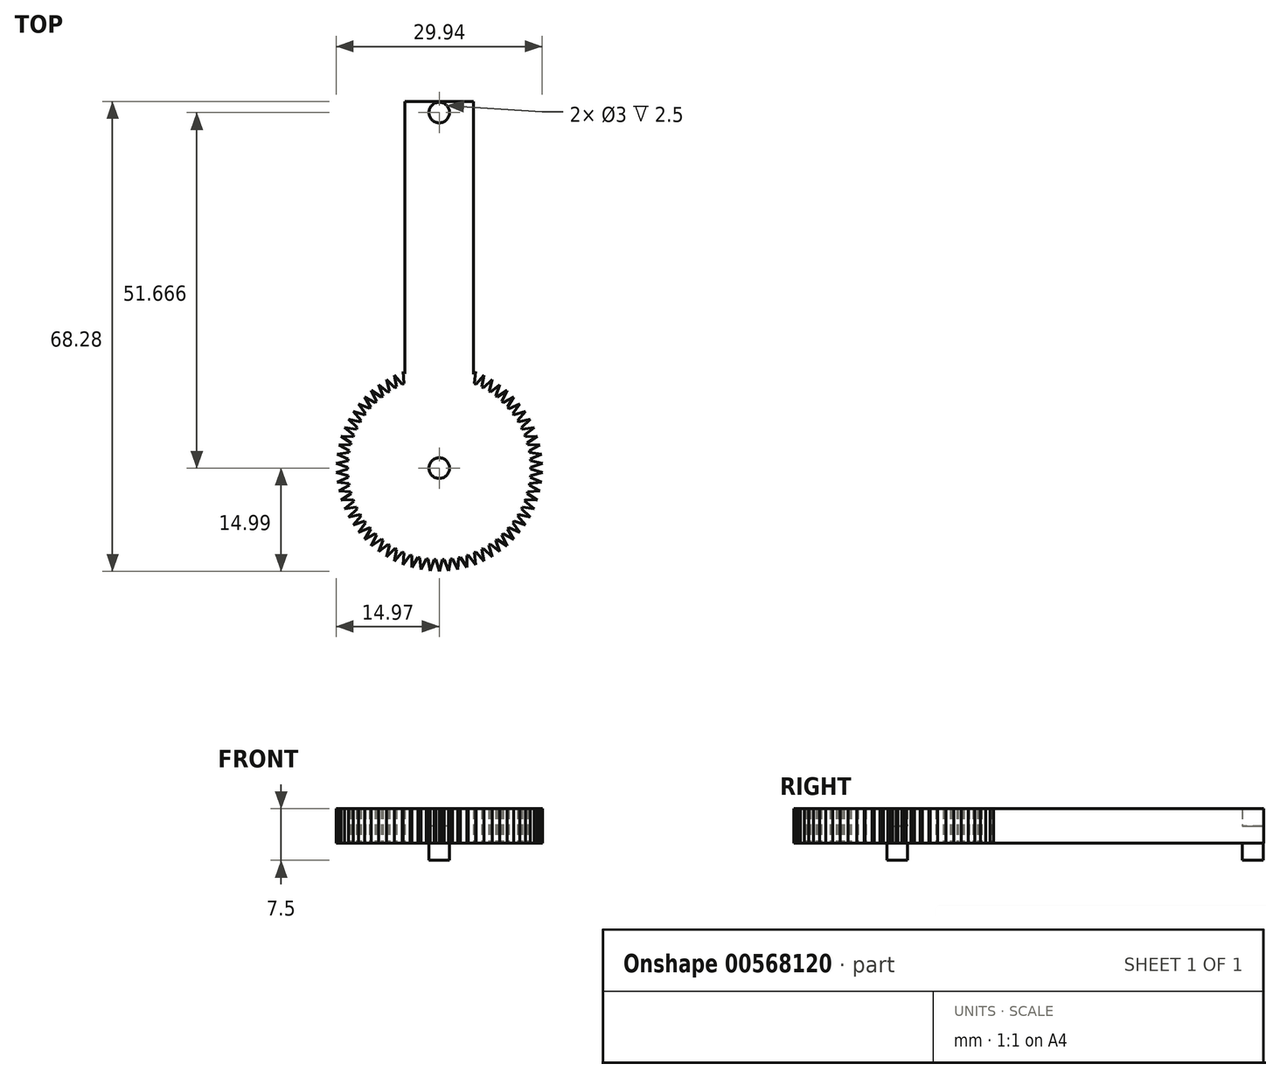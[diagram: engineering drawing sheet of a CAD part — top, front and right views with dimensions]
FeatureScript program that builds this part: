
annotation { "Feature Type Name" : "Feature", "Feature Type Description" : "" }
export const myFeature = defineFeature(function(context is Context, id is Id, definition is map)
    precondition{}
    {
        {
            var Q0;
            Q0=qCreatedBy(makeId("Top.planeOp"),FACE);
            var sketch = newSketch(context, id + "F0", { "sketchPlane" : qUnion([Q0])});
            skLineSegment(sketch, "E0.bottom", {"start": v(-5.03, 53.29) * mm, "end": v(4.97, 53.29) * mm});
            skLineSegment(sketch, "E0.left", {"start": v(-5.03, 53.29) * mm, "end": v(-5.03, 13.29) * mm});
            skLineSegment(sketch, "E0.right", {"start": v(4.97, 53.29) * mm, "end": v(4.97, 13.29) * mm});
            skCircle(sketch, "E1", {"center": v(0, -0.01) * mm, "radius": 15 * mm});
            skLineSegment(sketch, "E2.2.2", {"start": v(-2.84, 13) * mm, "end": v(-3.29, 12.92) * mm});
            skLineSegment(sketch, "E2.3.2", {"start": v(-3.99, 12.7) * mm, "end": v(-4.43, 12.57) * mm});
            skLineSegment(sketch, "E2.4.0", {"start": v(-5.27, 14.03) * mm, "end": v(-4.23, 12.61) * mm});
            skLineSegment(sketch, "E2.4.1", {"start": v(-5.27, 14.03) * mm, "end": v(-5.11, 12.28) * mm});
            skLineSegment(sketch, "E2.4.2", {"start": v(-5.11, 12.28) * mm, "end": v(-5.54, 12.12) * mm});
            skLineSegment(sketch, "E2.5.0", {"start": v(-6.5, 13.5) * mm, "end": v(-5.35, 12.18) * mm});
            skLineSegment(sketch, "E2.5.1", {"start": v(-6.5, 13.5) * mm, "end": v(-6.2, 11.78) * mm});
            skLineSegment(sketch, "E2.5.2", {"start": v(-6.2, 11.78) * mm, "end": v(-6.6, 11.58) * mm});
            skLineSegment(sketch, "E2.6.0", {"start": v(-7.69, 12.87) * mm, "end": v(-6.42, 11.66) * mm});
            skLineSegment(sketch, "E2.6.1", {"start": v(-7.69, 12.87) * mm, "end": v(-7.22, 11.17) * mm});
            skLineSegment(sketch, "E2.6.2", {"start": v(-7.22, 11.17) * mm, "end": v(-7.62, 10.94) * mm});
            skLineSegment(sketch, "E2.7.0", {"start": v(-8.8, 12.13) * mm, "end": v(-7.44, 11.03) * mm});
            skLineSegment(sketch, "E2.7.1", {"start": v(-8.8, 12.13) * mm, "end": v(-8.2, 10.48) * mm});
            skLineSegment(sketch, "E2.7.2", {"start": v(-8.2, 10.48) * mm, "end": v(-8.57, 10.21) * mm});
            skLineSegment(sketch, "E2.8.0", {"start": v(-9.86, 11.29) * mm, "end": v(-8.4, 10.32) * mm});
            skLineSegment(sketch, "E2.8.1", {"start": v(-9.86, 11.29) * mm, "end": v(-9.1, 9.7) * mm});
            skLineSegment(sketch, "E2.8.2", {"start": v(-9.1, 9.7) * mm, "end": v(-9.45, 9.4) * mm});
            skLineSegment(sketch, "E2.9.0", {"start": v(-10.83, 10.36) * mm, "end": v(-9.29, 9.53) * mm});
            skLineSegment(sketch, "E2.9.1", {"start": v(-10.83, 10.36) * mm, "end": v(-9.94, 8.85) * mm});
            skLineSegment(sketch, "E2.9.2", {"start": v(-9.94, 8.85) * mm, "end": v(-10.25, 8.52) * mm});
            skLineSegment(sketch, "E2.10.0", {"start": v(-11.72, 9.34) * mm, "end": v(-10.1, 8.66) * mm});
            skLineSegment(sketch, "E2.10.1", {"start": v(-11.72, 9.34) * mm, "end": v(-10.69, 7.92) * mm});
            skLineSegment(sketch, "E2.10.2", {"start": v(-10.69, 7.92) * mm, "end": v(-10.97, 7.57) * mm});
            skLineSegment(sketch, "E2.11.0", {"start": v(-12.5, 8.26) * mm, "end": v(-10.84, 7.72) * mm});
            skLineSegment(sketch, "E2.11.1", {"start": v(-12.5, 8.26) * mm, "end": v(-11.36, 6.93) * mm});
            skLineSegment(sketch, "E2.11.2", {"start": v(-11.36, 6.93) * mm, "end": v(-11.6, 6.55) * mm});
            skLineSegment(sketch, "E2.12.0", {"start": v(-13.2, 7.1) * mm, "end": v(-11.49, 6.71) * mm});
            skLineSegment(sketch, "E2.12.1", {"start": v(-13.2, 7.1) * mm, "end": v(-11.93, 5.89) * mm});
            skLineSegment(sketch, "E2.12.2", {"start": v(-11.93, 5.89) * mm, "end": v(-12.15, 5.49) * mm});
            skLineSegment(sketch, "E2.13.0", {"start": v(-13.78, 5.9) * mm, "end": v(-12.04, 5.66) * mm});
            skLineSegment(sketch, "E2.13.1", {"start": v(-13.78, 5.9) * mm, "end": v(-12.41, 4.8) * mm});
            skLineSegment(sketch, "E2.13.2", {"start": v(-12.41, 4.8) * mm, "end": v(-12.6, 4.37) * mm});
            skLineSegment(sketch, "E2.14.0", {"start": v(-14.25, 4.63) * mm, "end": v(-12.5, 4.56) * mm});
            skLineSegment(sketch, "E2.14.1", {"start": v(-14.25, 4.63) * mm, "end": v(-12.8, 3.66) * mm});
            skLineSegment(sketch, "E2.14.2", {"start": v(-12.8, 3.66) * mm, "end": v(-12.93, 3.23) * mm});
            skLineSegment(sketch, "E2.15.0", {"start": v(-14.61, 3.34) * mm, "end": v(-12.86, 3.42) * mm});
            skLineSegment(sketch, "E2.15.1", {"start": v(-14.61, 3.34) * mm, "end": v(-13.07, 2.5) * mm});
            skLineSegment(sketch, "E2.15.2", {"start": v(-13.07, 2.5) * mm, "end": v(-13.17, 2.06) * mm});
            skLineSegment(sketch, "E2.16.0", {"start": v(-14.85, 2.01) * mm, "end": v(-13.11, 2.25) * mm});
            skLineSegment(sketch, "E2.16.1", {"start": v(-14.85, 2.01) * mm, "end": v(-13.24, 1.32) * mm});
            skLineSegment(sketch, "E2.16.2", {"start": v(-13.24, 1.32) * mm, "end": v(-13.3, 0.87) * mm});
            skLineSegment(sketch, "E2.17.0", {"start": v(-14.97, 0.67) * mm, "end": v(-13.26, 1.06) * mm});
            skLineSegment(sketch, "E2.17.1", {"start": v(-14.97, 0.67) * mm, "end": v(-13.3, 0.13) * mm});
            skLineSegment(sketch, "E2.17.2", {"start": v(-13.3, 0.13) * mm, "end": v(-13.33, -0.33) * mm});
            skLineSegment(sketch, "E2.18.0", {"start": v(-14.97, -0.67) * mm, "end": v(-13.3, -0.13) * mm});
            skLineSegment(sketch, "E2.18.1", {"start": v(-14.97, -0.67) * mm, "end": v(-13.26, -1.06) * mm});
            skLineSegment(sketch, "E2.18.2", {"start": v(-13.26, -1.06) * mm, "end": v(-13.24, -1.52) * mm});
            skLineSegment(sketch, "E2.19.0", {"start": v(-14.85, -2.01) * mm, "end": v(-13.24, -1.32) * mm});
            skLineSegment(sketch, "E2.19.1", {"start": v(-14.85, -2.01) * mm, "end": v(-13.11, -2.25) * mm});
            skLineSegment(sketch, "E2.19.2", {"start": v(-13.11, -2.25) * mm, "end": v(-13.05, -2.7) * mm});
            skLineSegment(sketch, "E2.20.0", {"start": v(-14.61, -3.34) * mm, "end": v(-13.07, -2.5) * mm});
            skLineSegment(sketch, "E2.20.1", {"start": v(-14.61, -3.34) * mm, "end": v(-12.86, -3.42) * mm});
            skLineSegment(sketch, "E2.20.2", {"start": v(-12.86, -3.42) * mm, "end": v(-12.76, -3.86) * mm});
            skLineSegment(sketch, "E2.21.0", {"start": v(-14.25, -4.63) * mm, "end": v(-12.8, -3.66) * mm});
            skLineSegment(sketch, "E2.21.1", {"start": v(-14.25, -4.63) * mm, "end": v(-12.5, -4.56) * mm});
            skLineSegment(sketch, "E2.21.2", {"start": v(-12.5, -4.56) * mm, "end": v(-12.36, -4.99) * mm});
            skLineSegment(sketch, "E2.22.0", {"start": v(-13.78, -5.9) * mm, "end": v(-12.41, -4.8) * mm});
            skLineSegment(sketch, "E2.22.1", {"start": v(-13.78, -5.9) * mm, "end": v(-12.04, -5.66) * mm});
            skLineSegment(sketch, "E2.22.2", {"start": v(-12.04, -5.66) * mm, "end": v(-11.86, -6.08) * mm});
            skLineSegment(sketch, "E2.23.0", {"start": v(-13.2, -7.1) * mm, "end": v(-11.93, -5.89) * mm});
            skLineSegment(sketch, "E2.23.1", {"start": v(-13.2, -7.1) * mm, "end": v(-11.49, -6.71) * mm});
            skLineSegment(sketch, "E2.23.2", {"start": v(-11.49, -6.71) * mm, "end": v(-11.27, -7.12) * mm});
            skLineSegment(sketch, "E2.24.0", {"start": v(-12.5, -8.26) * mm, "end": v(-11.36, -6.93) * mm});
            skLineSegment(sketch, "E2.24.1", {"start": v(-12.5, -8.26) * mm, "end": v(-10.84, -7.72) * mm});
            skLineSegment(sketch, "E2.24.2", {"start": v(-10.84, -7.72) * mm, "end": v(-10.59, -8.1) * mm});
            skLineSegment(sketch, "E2.25.0", {"start": v(-11.72, -9.34) * mm, "end": v(-10.69, -7.92) * mm});
            skLineSegment(sketch, "E2.25.1", {"start": v(-11.72, -9.34) * mm, "end": v(-10.1, -8.66) * mm});
            skLineSegment(sketch, "E2.25.2", {"start": v(-10.1, -8.66) * mm, "end": v(-9.82, -9.01) * mm});
            skLineSegment(sketch, "E2.26.0", {"start": v(-10.83, -10.36) * mm, "end": v(-9.94, -8.85) * mm});
            skLineSegment(sketch, "E2.26.1", {"start": v(-10.83, -10.36) * mm, "end": v(-9.29, -9.53) * mm});
            skLineSegment(sketch, "E2.26.2", {"start": v(-9.29, -9.53) * mm, "end": v(-8.97, -9.86) * mm});
            skLineSegment(sketch, "E2.27.0", {"start": v(-9.86, -11.29) * mm, "end": v(-9.1, -9.7) * mm});
            skLineSegment(sketch, "E2.27.1", {"start": v(-9.86, -11.29) * mm, "end": v(-8.4, -10.32) * mm});
            skLineSegment(sketch, "E2.27.2", {"start": v(-8.4, -10.32) * mm, "end": v(-8.05, -10.62) * mm});
            skLineSegment(sketch, "E2.28.0", {"start": v(-8.8, -12.13) * mm, "end": v(-8.2, -10.48) * mm});
            skLineSegment(sketch, "E2.28.1", {"start": v(-8.8, -12.13) * mm, "end": v(-7.44, -11.03) * mm});
            skLineSegment(sketch, "E2.28.2", {"start": v(-7.44, -11.03) * mm, "end": v(-7.07, -11.3) * mm});
            skLineSegment(sketch, "E2.29.0", {"start": v(-7.69, -12.87) * mm, "end": v(-7.22, -11.17) * mm});
            skLineSegment(sketch, "E2.29.1", {"start": v(-7.69, -12.87) * mm, "end": v(-6.42, -11.66) * mm});
            skLineSegment(sketch, "E2.29.2", {"start": v(-6.42, -11.66) * mm, "end": v(-6.03, -11.9) * mm});
            skLineSegment(sketch, "E2.30.0", {"start": v(-6.5, -13.5) * mm, "end": v(-6.2, -11.78) * mm});
            skLineSegment(sketch, "E2.30.1", {"start": v(-6.5, -13.5) * mm, "end": v(-5.35, -12.18) * mm});
            skLineSegment(sketch, "E2.30.2", {"start": v(-5.35, -12.18) * mm, "end": v(-4.94, -12.38) * mm});
            skLineSegment(sketch, "E2.31.0", {"start": v(-5.27, -14.03) * mm, "end": v(-5.11, -12.28) * mm});
            skLineSegment(sketch, "E2.31.1", {"start": v(-5.27, -14.03) * mm, "end": v(-4.23, -12.61) * mm});
            skLineSegment(sketch, "E2.31.2", {"start": v(-4.23, -12.61) * mm, "end": v(-3.8, -12.77) * mm});
            skLineSegment(sketch, "E2.32.0", {"start": v(-3.99, -14.45) * mm, "end": v(-3.99, -12.7) * mm});
            skLineSegment(sketch, "E2.32.1", {"start": v(-3.99, -14.45) * mm, "end": v(-3.09, -12.94) * mm});
            skLineSegment(sketch, "E2.32.2", {"start": v(-3.09, -12.94) * mm, "end": v(-2.65, -13.06) * mm});
            skLineSegment(sketch, "E2.33.0", {"start": v(-2.68, -14.75) * mm, "end": v(-2.84, -13) * mm});
            skLineSegment(sketch, "E2.33.1", {"start": v(-2.68, -14.75) * mm, "end": v(-1.91, -13.17) * mm});
            skLineSegment(sketch, "E2.33.2", {"start": v(-1.91, -13.17) * mm, "end": v(-1.46, -13.25) * mm});
            skLineSegment(sketch, "E2.34.0", {"start": v(-1.34, -14.93) * mm, "end": v(-1.66, -13.2) * mm});
            skLineSegment(sketch, "E2.34.1", {"start": v(-1.34, -14.93) * mm, "end": v(-0.73, -13.29) * mm});
            skLineSegment(sketch, "E2.34.2", {"start": v(-0.73, -13.29) * mm, "end": v(-0.27, -13.33) * mm});
            skLineSegment(sketch, "E2.35.0", {"start": v(0, -14.99) * mm, "end": v(-0.47, -13.3) * mm});
            skLineSegment(sketch, "E2.35.1", {"start": v(0, -14.99) * mm, "end": v(0.47, -13.3) * mm});
            skLineSegment(sketch, "E2.35.2", {"start": v(0.47, -13.3) * mm, "end": v(0.93, -13.3) * mm});
            skLineSegment(sketch, "E2.36.0", {"start": v(1.34, -14.93) * mm, "end": v(0.73, -13.29) * mm});
            skLineSegment(sketch, "E2.36.1", {"start": v(1.34, -14.93) * mm, "end": v(1.66, -13.2) * mm});
            skLineSegment(sketch, "E2.36.2", {"start": v(1.66, -13.2) * mm, "end": v(2.11, -13.16) * mm});
            skLineSegment(sketch, "E2.37.0", {"start": v(2.68, -14.75) * mm, "end": v(1.91, -13.17) * mm});
            skLineSegment(sketch, "E2.37.1", {"start": v(2.68, -14.75) * mm, "end": v(2.84, -13) * mm});
            skLineSegment(sketch, "E2.37.2", {"start": v(2.84, -13) * mm, "end": v(3.29, -12.92) * mm});
            skLineSegment(sketch, "E2.38.0", {"start": v(3.99, -14.45) * mm, "end": v(3.09, -12.94) * mm});
            skLineSegment(sketch, "E2.38.1", {"start": v(3.99, -14.45) * mm, "end": v(3.99, -12.7) * mm});
            skLineSegment(sketch, "E2.38.2", {"start": v(3.99, -12.7) * mm, "end": v(4.43, -12.57) * mm});
            skLineSegment(sketch, "E2.39.0", {"start": v(5.27, -14.03) * mm, "end": v(4.23, -12.61) * mm});
            skLineSegment(sketch, "E2.39.1", {"start": v(5.27, -14.03) * mm, "end": v(5.11, -12.28) * mm});
            skLineSegment(sketch, "E2.39.2", {"start": v(5.11, -12.28) * mm, "end": v(5.54, -12.12) * mm});
            skLineSegment(sketch, "E2.40.0", {"start": v(6.5, -13.5) * mm, "end": v(5.35, -12.18) * mm});
            skLineSegment(sketch, "E2.40.1", {"start": v(6.5, -13.5) * mm, "end": v(6.2, -11.78) * mm});
            skLineSegment(sketch, "E2.40.2", {"start": v(6.2, -11.78) * mm, "end": v(6.6, -11.58) * mm});
            skLineSegment(sketch, "E2.41.0", {"start": v(7.69, -12.87) * mm, "end": v(6.42, -11.66) * mm});
            skLineSegment(sketch, "E2.41.1", {"start": v(7.69, -12.87) * mm, "end": v(7.22, -11.17) * mm});
            skLineSegment(sketch, "E2.41.2", {"start": v(7.22, -11.17) * mm, "end": v(7.62, -10.94) * mm});
            skLineSegment(sketch, "E2.42.0", {"start": v(8.8, -12.13) * mm, "end": v(7.44, -11.03) * mm});
            skLineSegment(sketch, "E2.42.1", {"start": v(8.8, -12.13) * mm, "end": v(8.2, -10.48) * mm});
            skLineSegment(sketch, "E2.42.2", {"start": v(8.2, -10.48) * mm, "end": v(8.57, -10.21) * mm});
            skLineSegment(sketch, "E2.43.0", {"start": v(9.86, -11.29) * mm, "end": v(8.4, -10.32) * mm});
            skLineSegment(sketch, "E2.43.1", {"start": v(9.86, -11.29) * mm, "end": v(9.1, -9.7) * mm});
            skLineSegment(sketch, "E2.43.2", {"start": v(9.1, -9.7) * mm, "end": v(9.45, -9.4) * mm});
            skLineSegment(sketch, "E2.44.0", {"start": v(10.83, -10.36) * mm, "end": v(9.29, -9.53) * mm});
            skLineSegment(sketch, "E2.44.1", {"start": v(10.83, -10.36) * mm, "end": v(9.94, -8.85) * mm});
            skLineSegment(sketch, "E2.44.2", {"start": v(9.94, -8.85) * mm, "end": v(10.25, -8.52) * mm});
            skLineSegment(sketch, "E2.45.0", {"start": v(11.72, -9.34) * mm, "end": v(10.1, -8.66) * mm});
            skLineSegment(sketch, "E2.45.1", {"start": v(11.72, -9.34) * mm, "end": v(10.69, -7.92) * mm});
            skLineSegment(sketch, "E2.45.2", {"start": v(10.69, -7.92) * mm, "end": v(10.97, -7.57) * mm});
            skLineSegment(sketch, "E2.46.0", {"start": v(12.5, -8.26) * mm, "end": v(10.84, -7.72) * mm});
            skLineSegment(sketch, "E2.46.1", {"start": v(12.5, -8.26) * mm, "end": v(11.36, -6.93) * mm});
            skLineSegment(sketch, "E2.46.2", {"start": v(11.36, -6.93) * mm, "end": v(11.6, -6.55) * mm});
            skLineSegment(sketch, "E2.47.0", {"start": v(13.2, -7.1) * mm, "end": v(11.49, -6.71) * mm});
            skLineSegment(sketch, "E2.47.1", {"start": v(13.2, -7.1) * mm, "end": v(11.93, -5.89) * mm});
            skLineSegment(sketch, "E2.47.2", {"start": v(11.93, -5.89) * mm, "end": v(12.15, -5.49) * mm});
            skLineSegment(sketch, "E2.48.0", {"start": v(13.78, -5.9) * mm, "end": v(12.04, -5.66) * mm});
            skLineSegment(sketch, "E2.48.1", {"start": v(13.78, -5.9) * mm, "end": v(12.41, -4.8) * mm});
            skLineSegment(sketch, "E2.48.2", {"start": v(12.41, -4.8) * mm, "end": v(12.6, -4.37) * mm});
            skLineSegment(sketch, "E2.49.0", {"start": v(14.25, -4.63) * mm, "end": v(12.5, -4.56) * mm});
            skLineSegment(sketch, "E2.49.1", {"start": v(14.25, -4.63) * mm, "end": v(12.8, -3.66) * mm});
            skLineSegment(sketch, "E2.49.2", {"start": v(12.8, -3.66) * mm, "end": v(12.93, -3.23) * mm});
            skLineSegment(sketch, "E2.50.0", {"start": v(14.61, -3.34) * mm, "end": v(12.86, -3.42) * mm});
            skLineSegment(sketch, "E2.50.1", {"start": v(14.61, -3.34) * mm, "end": v(13.07, -2.5) * mm});
            skLineSegment(sketch, "E2.50.2", {"start": v(13.07, -2.5) * mm, "end": v(13.17, -2.06) * mm});
            skLineSegment(sketch, "E2.51.0", {"start": v(14.85, -2.01) * mm, "end": v(13.11, -2.25) * mm});
            skLineSegment(sketch, "E2.51.1", {"start": v(14.85, -2.01) * mm, "end": v(13.24, -1.32) * mm});
            skLineSegment(sketch, "E2.51.2", {"start": v(13.24, -1.32) * mm, "end": v(13.3, -0.87) * mm});
            skLineSegment(sketch, "E2.52.0", {"start": v(14.97, -0.67) * mm, "end": v(13.26, -1.06) * mm});
            skLineSegment(sketch, "E2.52.1", {"start": v(14.97, -0.67) * mm, "end": v(13.3, -0.13) * mm});
            skLineSegment(sketch, "E2.52.2", {"start": v(13.3, -0.13) * mm, "end": v(13.33, 0.33) * mm});
            skLineSegment(sketch, "E2.53.0", {"start": v(14.97, 0.67) * mm, "end": v(13.3, 0.13) * mm});
            skLineSegment(sketch, "E2.53.1", {"start": v(14.97, 0.67) * mm, "end": v(13.26, 1.06) * mm});
            skLineSegment(sketch, "E2.53.2", {"start": v(13.26, 1.06) * mm, "end": v(13.24, 1.52) * mm});
            skLineSegment(sketch, "E2.54.0", {"start": v(14.85, 2.01) * mm, "end": v(13.24, 1.32) * mm});
            skLineSegment(sketch, "E2.54.1", {"start": v(14.85, 2.01) * mm, "end": v(13.11, 2.25) * mm});
            skLineSegment(sketch, "E2.54.2", {"start": v(13.11, 2.25) * mm, "end": v(13.05, 2.7) * mm});
            skLineSegment(sketch, "E2.55.0", {"start": v(14.61, 3.34) * mm, "end": v(13.07, 2.5) * mm});
            skLineSegment(sketch, "E2.55.1", {"start": v(14.61, 3.34) * mm, "end": v(12.86, 3.42) * mm});
            skLineSegment(sketch, "E2.55.2", {"start": v(12.86, 3.42) * mm, "end": v(12.76, 3.86) * mm});
            skLineSegment(sketch, "E2.56.0", {"start": v(14.25, 4.63) * mm, "end": v(12.8, 3.66) * mm});
            skLineSegment(sketch, "E2.56.1", {"start": v(14.25, 4.63) * mm, "end": v(12.5, 4.56) * mm});
            skLineSegment(sketch, "E2.56.2", {"start": v(12.5, 4.56) * mm, "end": v(12.36, 4.99) * mm});
            skLineSegment(sketch, "E2.57.0", {"start": v(13.78, 5.9) * mm, "end": v(12.41, 4.8) * mm});
            skLineSegment(sketch, "E2.57.1", {"start": v(13.78, 5.9) * mm, "end": v(12.04, 5.66) * mm});
            skLineSegment(sketch, "E2.57.2", {"start": v(12.04, 5.66) * mm, "end": v(11.86, 6.08) * mm});
            skLineSegment(sketch, "E2.58.0", {"start": v(13.2, 7.1) * mm, "end": v(11.93, 5.89) * mm});
            skLineSegment(sketch, "E2.58.1", {"start": v(13.2, 7.1) * mm, "end": v(11.49, 6.71) * mm});
            skLineSegment(sketch, "E2.58.2", {"start": v(11.49, 6.71) * mm, "end": v(11.27, 7.12) * mm});
            skLineSegment(sketch, "E2.59.0", {"start": v(12.5, 8.26) * mm, "end": v(11.36, 6.93) * mm});
            skLineSegment(sketch, "E2.59.1", {"start": v(12.5, 8.26) * mm, "end": v(10.84, 7.72) * mm});
            skLineSegment(sketch, "E2.59.2", {"start": v(10.84, 7.72) * mm, "end": v(10.59, 8.1) * mm});
            skLineSegment(sketch, "E2.60.0", {"start": v(11.72, 9.34) * mm, "end": v(10.69, 7.92) * mm});
            skLineSegment(sketch, "E2.60.1", {"start": v(11.72, 9.34) * mm, "end": v(10.1, 8.66) * mm});
            skLineSegment(sketch, "E2.60.2", {"start": v(10.1, 8.66) * mm, "end": v(9.82, 9.01) * mm});
            skLineSegment(sketch, "E2.61.0", {"start": v(10.83, 10.36) * mm, "end": v(9.94, 8.85) * mm});
            skLineSegment(sketch, "E2.61.1", {"start": v(10.83, 10.36) * mm, "end": v(9.29, 9.53) * mm});
            skLineSegment(sketch, "E2.61.2", {"start": v(9.29, 9.53) * mm, "end": v(8.97, 9.86) * mm});
            skLineSegment(sketch, "E2.62.0", {"start": v(9.86, 11.29) * mm, "end": v(9.1, 9.7) * mm});
            skLineSegment(sketch, "E2.62.1", {"start": v(9.86, 11.29) * mm, "end": v(8.4, 10.32) * mm});
            skLineSegment(sketch, "E2.62.2", {"start": v(8.4, 10.32) * mm, "end": v(8.05, 10.62) * mm});
            skLineSegment(sketch, "E2.63.0", {"start": v(8.8, 12.13) * mm, "end": v(8.2, 10.48) * mm});
            skLineSegment(sketch, "E2.63.1", {"start": v(8.8, 12.13) * mm, "end": v(7.44, 11.03) * mm});
            skLineSegment(sketch, "E2.63.2", {"start": v(7.44, 11.03) * mm, "end": v(7.07, 11.3) * mm});
            skLineSegment(sketch, "E2.64.0", {"start": v(7.69, 12.87) * mm, "end": v(7.22, 11.17) * mm});
            skLineSegment(sketch, "E2.64.1", {"start": v(7.69, 12.87) * mm, "end": v(6.42, 11.66) * mm});
            skLineSegment(sketch, "E2.64.2", {"start": v(6.42, 11.66) * mm, "end": v(6.03, 11.9) * mm});
            skLineSegment(sketch, "E2.65.0", {"start": v(6.5, 13.5) * mm, "end": v(6.2, 11.78) * mm});
            skLineSegment(sketch, "E2.65.1", {"start": v(6.5, 13.5) * mm, "end": v(5.35, 12.18) * mm});
            skLineSegment(sketch, "E2.65.2", {"start": v(5.35, 12.18) * mm, "end": v(4.94, 12.38) * mm});
            skLineSegment(sketch, "E2.66.0", {"start": v(5.27, 14.03) * mm, "end": v(5.11, 12.28) * mm});
            skLineSegment(sketch, "E2.66.1", {"start": v(5.27, 14.03) * mm, "end": v(4.23, 12.61) * mm});
            skLineSegment(sketch, "E2.66.2", {"start": v(4.23, 12.61) * mm, "end": v(3.8, 12.77) * mm});
            skLineSegment(sketch, "E2.67.0", {"start": v(3.99, 14.45) * mm, "end": v(3.99, 12.7) * mm});
            skLineSegment(sketch, "E2.67.1", {"start": v(3.99, 14.45) * mm, "end": v(3.09, 12.94) * mm});
            skPoint(sketch, "E2.center", {"position": v(0, 0) * mm});
            skCircle(sketch, "E3", {"center": v(0, 51.67) * mm, "radius": 1.5 * mm});
            skCircle(sketch, "E4", {"center": v(0, 0) * mm, "radius": 1.5 * mm});
            skSolve(sketch);
        }
        {
            var Q0;
            {var subQ184=sQuery(id+"F0.wireOp",EDGE,"972eCkCt-WNXn-4gxg-s8lq-SkAAgc3m8y7d");Q0=makeQuery(id+"F0.imprint","IMPRINT",FACE,{"disambiguationData":[TD([[makeQuery(id+"F0.imprint","IMPRINT",EDGE,{"derivedFrom":subQ184}),1.0]])]});}
            var Q1;
            Q1=makeQuery(id+"F0.imprint","IMPRINT",FACE,{"disambiguationData":[TD([[makeQuery(id+"F0.imprint","IMPRINT",EDGE,{"derivedFrom":sQuery(id+"F0.wireOp",EDGE,"E0.bottom")}),-1.0]])]});
            var Q2;
            {var subQ88=sQuery(id+"F0.wireOp",EDGE,"E2.4.1");Q2=makeQuery(id+"F0.imprint","IMPRINT",FACE,{"disambiguationData":[TD([[makeQuery(id+"F0.imprint","IMPRINT",EDGE,{"derivedFrom":subQ88}),1.0]])]});}
            extrude(context, id + "F1", {"entities" : qUnion([Q0, Q1, Q2]), "endBound" : BoundingType.SYMMETRIC, "depth" : 5 * mm, "offsetDistance" : 25 * mm});
        }
        {
            var Q0;
            Q0=sQuery(id+"F0.wireOp",EDGE,"E0.right");
            var Q1;
            Q1=sQuery(id+"F0.wireOp",EDGE,"E0.left");
            var Q2;
            Q2=sQuery(id+"F0.wireOp",EDGE,"E0.top");
            var Q3;
            Q3=sQuery(id+"F0.wireOp",EDGE,"E0.bottom");
            extrude(context, id + "F2", {"bodyType" : ToolBodyType.SURFACE, "surfaceEntities" : qUnion([Q0, Q1, Q2, Q3]), "endBound" : BoundingType.SYMMETRIC, "depth" : 5 * mm, "offsetDistance" : 25 * mm});
        }
        {
            var Q0;
            Q0=makeQuery(id+"F0.imprint","IMPRINT",FACE,{"disambiguationData":[TD([[makeQuery(id+"F0.imprint","IMPRINT",EDGE,{"derivedFrom":sQuery(id+"F0.wireOp",EDGE,"E3")}),1.0]])]});
            var Q1;
            Q1=makeQuery(id+"F0.imprint","IMPRINT",FACE,{"disambiguationData":[TD([[makeQuery(id+"F0.imprint","IMPRINT",EDGE,{"derivedFrom":sQuery(id+"F0.wireOp",EDGE,"E4")}),1.0]])]});
            extrude(context, id + "F3", {"entities" : qUnion([Q0, Q1]), "operationType" : NewBodyOperationType.ADD, "oppositeDirection" : true, "depth" : 5 * mm, "offsetDistance" : 25 * mm});
        }
    });
